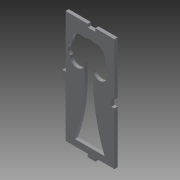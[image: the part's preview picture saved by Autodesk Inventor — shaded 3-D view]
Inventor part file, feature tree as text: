
AUTODESK INVENTOR PART (.ipt)
format: ipt  version: 2015 (Build 190159000, 159)  size: 164,352 bytes
history: native  units: in
note: dims shown in document units (in); Inventor stores cm internally (conversion verified against a paired STEP export)
features: extrude x4, sketch x4
ambient origin geometry x8: Origin, YZ Plane, XZ Plane, XY Plane, X Axis, Y Axis, Z Axis, Center Point
bodies: Solid1 (feature_tree)
feature tree (8):
  extrude  "Extrusion1"  Depth=1.959in
  sketch  "Sketch2"  dims[d2=0.125in d3=0.0in d4=0.15in]
  extrude  "Extrusion2"  Depth=0.125in
  extrude  "Extrusion3"  Depth=0.125in
  sketch  "Sketch3"  dims[d5=0.3in d6=0.125in]
  extrude  "Extrusion4"  Depth=0.3in
  sketch  "Sketch1"  dims[d0=4.5in d1=1.959in]
  sketch  "Sketch4"  dims[d7=0.15in d8=0.3in d9=0.125in d13=0.3in d15=0.125in d16=0.125in d17=0.0in d18=0.125in d19=0.0in d20=0.3in d22=0.125in d23=2.8125in d24=0.25in d25=7.0in d26=0.25in d28=7.0in d29=1.041in d30=2.8125in d31=1.0in d32=0.0in d33=0.15in d34=1.041in d35=1.041in d36=0.15in]
